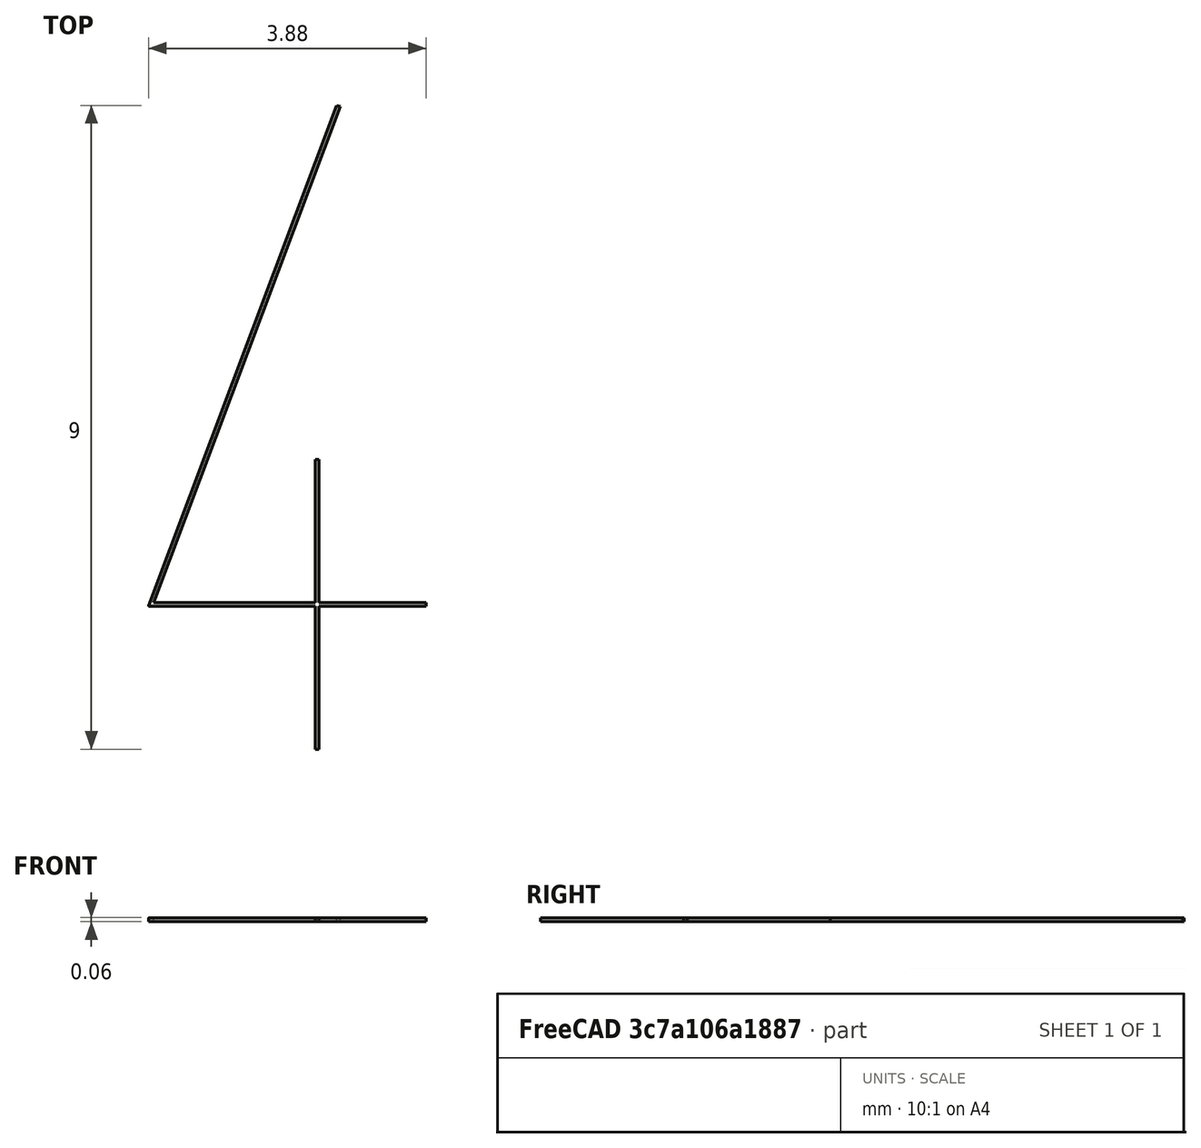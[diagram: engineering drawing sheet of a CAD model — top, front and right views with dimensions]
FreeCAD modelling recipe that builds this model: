
FCSTD DOCUMENT  (FreeCAD 0.16R6712 (Git))
Label: 4t
License: All rights reserved
LicenseURL: http://en.wikipedia.org/wiki/All_rights_reserved
objects: Sketcher::SketchObject×1, PartDesign::Pad×1, Mesh::Feature×1
note: 3 computed .brp shape members not serialized (recipe doc carries the construction recipe); baked Part::Feature solids carry a one-line shape summary decoded from their .brp

FEATURE [Sketcher::SketchObject] Sketch
  sketch-geometry (15):
    g0: LineSegment StartX=0.753204 StartY=9 StartZ=0 EndX=-1.87827 EndY=2.00696 EndZ=0
    g1: LineSegment StartX=0.8 StartY=8.98239 StartZ=0 EndX=-1.80865 EndY=2.05 EndZ=0
    g2: LineSegment StartX=-1.87345 StartY=2 StartZ=0 EndX=0.45 EndY=2 EndZ=0
    g3: LineSegment StartX=-1.80865 StartY=2.05 StartZ=0 EndX=0.45 EndY=2.05 EndZ=0
    g4: LineSegment StartX=0.753204 StartY=9 StartZ=0 EndX=0.8 EndY=8.98239 EndZ=0
    g5: LineSegment StartX=0.45 StartY=4.05 StartZ=0 EndX=0.5 EndY=4.05 EndZ=0
    g6: LineSegment StartX=0.5 StartY=4.05 StartZ=0 EndX=0.5 EndY=2.05 EndZ=0
    g7: LineSegment StartX=0.5 StartY=0 StartZ=0 EndX=0.45 EndY=0 EndZ=0
    g8: LineSegment StartX=0.45 StartY=0 StartZ=0 EndX=0.45 EndY=2 EndZ=0
    g9: LineSegment StartX=0.5 StartY=2 StartZ=0 EndX=0.5 EndY=0 EndZ=0
    g10: LineSegment StartX=0.45 StartY=2.05 StartZ=0 EndX=0.45 EndY=4.05 EndZ=0
    g11: LineSegment StartX=0.5 StartY=2.05 StartZ=0 EndX=2 EndY=2.05 EndZ=0
    g12: LineSegment StartX=0.5 StartY=2 StartZ=0 EndX=2 EndY=2 EndZ=0
    g13: LineSegment StartX=2 StartY=2.05 StartZ=0 EndX=2 EndY=2 EndZ=0
    g14: ArcOfCircle CenterX=-1.87345 CenterY=2.00515 CenterZ=0 NormalX=0 NormalY=0 NormalZ=1 Radius=0.00515052 StartAngle=2.78168 EndAngle=4.71239
  constraints (40):
    c: Horizontal(g2)
    c: Horizontal(g3)
    c: Coincident(g4,g1)
    c: Coincident(g1,g3)
    c: Perpendicular(g1,g4)
    c: Coincident(g0,g4)
    c: Distance(g0,g1) = 0.05
    c: Distance(g11,g12) = 0.05
    c: Parallel(g0,g1)
    c: Coincident(g5,g6)
    c: Coincident(g9,g7)
    c: Coincident(g7,g8)
    c: Coincident(g10,g5)
    c: Horizontal(g5)
    c: Horizontal(g7)
    c: Vertical(g6)
    c: Vertical(g8)
    c: Coincident(g3,g10)
    c: Coincident(g11,g6)
    c: Tangent(g3,g11)
    c: Coincident(g2,g8)
    c: Coincident(g12,g9)
    c: Tangent(g2,g12)
    c: Distance(g6,g5) = 2
    c: Coincident(g13,g11)
    c: Coincident(g13,g12)
    c: Vertical(g13)
    c: PointOnObject(g7,g-1)
    c: Distance(g7,g12) = 2
    c: DistanceY(g-1,g0) = 9
    c: DistanceX(g-2,g1) = 0.8
    c: Tangent(g0,g14) = -1.5708
    c: Tangent(g2,g14) = -1.5708
    c: DistanceX(g-2,g12) = 2
    c: Distance(g11,g6) = 1.5
    c: Distance(g12,g9) = 1.5
    c: Vertical(g9)
    c: DistanceX(g5,g5) = 0.05
    c: DistanceX(g7,g7) = 0.05
    c: Vertical(g10)
FEATURE [PartDesign::Pad] Pad
  Length = 0.05
  Length2 = 100
  Midplane = true
  Sketch = -> Sketch
  Type = 0
FEATURE [Mesh::Feature] Mesh  label="Pad (Meshed)"
